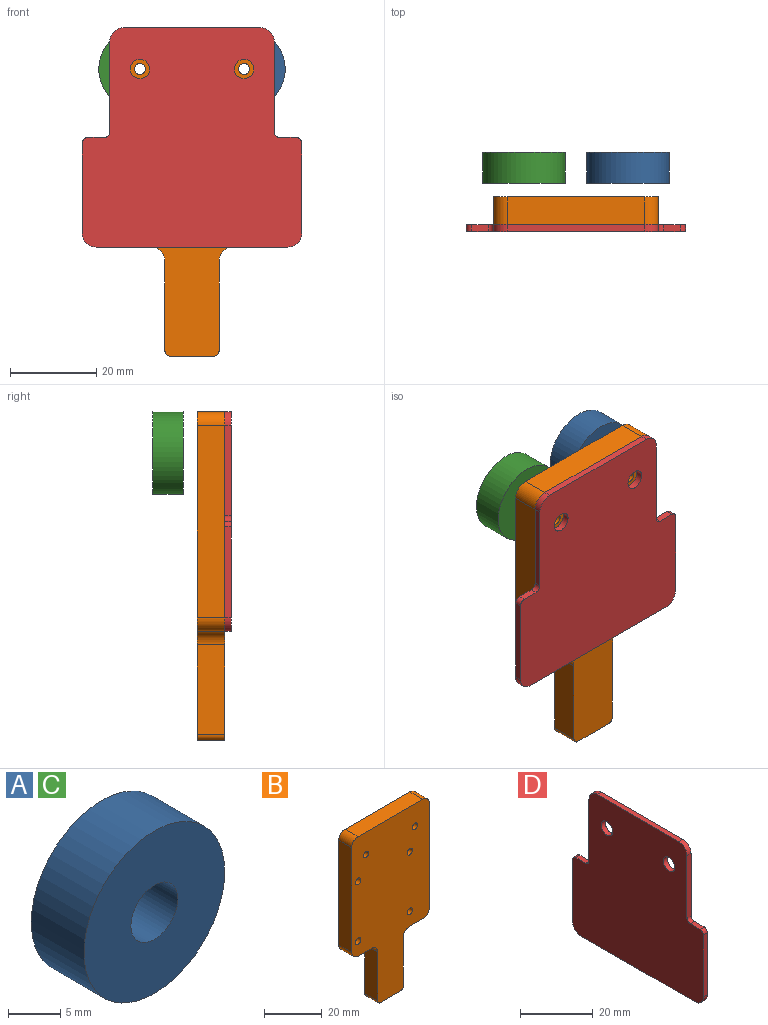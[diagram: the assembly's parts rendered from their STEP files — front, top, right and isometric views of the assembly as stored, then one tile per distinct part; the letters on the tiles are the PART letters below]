
ASSEMBLY  parts=4 mates=3
PART A: 4 faces, bbox 19.1x7.1x19.1 mm
  f0: cylinder r=3.17mm len=7.14mm, axis (0,1,0), area 142.4mm2, adj f2,f3
  f1: cylinder r=9.53mm len=19.05mm, axis (0,1,0), area 427.2mm2, adj f2,f3
  f2: plane 19.05x19.05mm, normal (0,-1,0), area 253.4mm2, adj f0,f1
  f3: plane 19.05x19.05mm, normal (0,1,0), area 253.4mm2, adj f0,f1
PART B: 24 faces, bbox 38.1x6.4x76.1 mm
  f0: cylinder r=3.17mm len=6.35mm, axis (0,1,0), area 31.7mm2, adj f1,f15,f16,f17
  f1: plane 6.41x6.35mm, normal (0,0,-1), area 40.7mm2, adj f0,f2,f16,f17
  f2: cylinder r=3.17mm len=6.35mm, axis (0,1,0), area 31.7mm2, adj f1,f3,f16,f17
  f3: plane 44.45x6.35mm, normal (1,0,0), area 282.3mm2, adj f2,f4,f16,f17
  f4: cylinder r=3.17mm len=6.35mm, axis (0,1,0), area 31.7mm2, adj f3,f5,f16,f17
  f5: plane 31.75x6.35mm, normal (0,0,1), area 201.6mm2, adj f4,f6,f16,f17
  f6: cylinder r=3.17mm len=6.35mm, axis (0,1,0), area 31.7mm2, adj f5,f7,f16,f17
  f7: plane 44.45x6.35mm, normal (-1,0,0), area 282.3mm2, adj f6,f8,f16,f17
  f8: cylinder r=3.17mm len=6.35mm, axis (0,1,0), area 31.7mm2, adj f7,f9,f16,f17
  f9: plane 6.41x6.35mm, normal (0,0,-1), area 40.7mm2, adj f8,f10,f16,f17
  f10: cylinder r=3.17mm len=6.35mm, axis (0,1,0), area 31.7mm2, adj f9,f11,f16,f17
  f11: plane 20.83x6.35mm, normal (-1,0,0), area 132.3mm2, adj f10,f12,f16,f17
  f12: cylinder r=1.27mm len=6.35mm, axis (0,1,0), area 12.7mm2, adj f11,f13,f16,f17
  f13: plane 10.03x6.35mm, normal (0,0,-1), area 63.7mm2, adj f12,f14,f16,f17
  f14: cylinder r=1.27mm len=6.35mm, axis (0,1,0), area 12.7mm2, adj f13,f15,f16,f17
  f15: plane 20.83x6.35mm, normal (1,0,0), area 132.3mm2, adj f0,f14,f16,f17
  f16: plane 76.07x38.1mm, normal (0,-1,0), area 2215.1mm2, adj f0,f1,f2,f3,f4,f5,f6,f7
  f17: plane 76.07x38.1mm, normal (0,1,0), area 2215.1mm2, adj f0,f1,f2,f3,f4,f5,f6,f7
  f18: cylinder r=1.27mm len=6.35mm, axis (0,1,0), area 50.7mm2, adj f16,f17
  f19: cylinder r=1.27mm len=6.35mm, axis (0,1,0), area 50.7mm2, adj f16,f17
  f20: cylinder r=1.35mm len=6.35mm, axis (0,-1,0), area 54mm2, adj f16,f17
  f21: cylinder r=1.35mm len=6.35mm, axis (0,-1,0), area 54mm2, adj f16,f17
  f22: cylinder r=1.35mm len=6.35mm, axis (0,-1,0), area 54mm2, adj f16,f17
  f23: cylinder r=1.35mm len=6.35mm, axis (0,-1,0), area 54mm2, adj f16,f17
PART C: same geometry as A
PART D: 20 faces, bbox 1.6x50.8x50.8 mm
  f0: plane 20.96x1.59mm, normal (0,1,0), area 33.3mm2, adj f1,f15,f16,f17
  f1: cylinder r=3.17mm len=3.18mm, axis (-1,0,0), area 7.9mm2, adj f0,f2,f16,f17
  f2: plane 31.75x1.59mm, normal (0,0,1), area 50.4mm2, adj f1,f3,f16,f17
  f3: cylinder r=3.17mm len=3.18mm, axis (-1,0,0), area 7.9mm2, adj f2,f4,f16,f17
  f4: plane 20.96x1.59mm, normal (0,-1,0), area 33.3mm2, adj f3,f5,f16,f17
  f5: cylinder r=1.27mm len=1.59mm, axis (-1,0,0), area 3.2mm2, adj f4,f6,f16,f17
  f6: plane 3.81x1.59mm, normal (0,0,1), area 6mm2, adj f5,f7,f16,f17
  f7: cylinder r=1.27mm len=1.59mm, axis (-1,0,0), area 3.2mm2, adj f6,f8,f16,f17
  f8: plane 20.96x1.59mm, normal (0,-1,0), area 33.3mm2, adj f7,f9,f16,f17
  f9: cylinder r=3.17mm len=3.18mm, axis (-1,0,0), area 7.9mm2, adj f8,f10,f16,f17
  f10: plane 44.45x1.59mm, normal (0,0,-1), area 70.6mm2, adj f9,f11,f16,f17
  f11: cylinder r=3.17mm len=3.18mm, axis (-1,0,0), area 7.9mm2, adj f10,f12,f16,f17
  f12: plane 20.96x1.59mm, normal (0,1,0), area 33.3mm2, adj f11,f13,f16,f17
  f13: cylinder r=1.27mm len=1.59mm, axis (-1,0,0), area 3.2mm2, adj f12,f14,f16,f17
  f14: plane 3.81x1.59mm, normal (0,0,1), area 6mm2, adj f13,f15,f16,f17
  f15: cylinder r=1.27mm len=1.59mm, axis (-1,0,0), area 3.2mm2, adj f0,f14,f16,f17
  f16: plane 50.8x50.8mm, normal (1,0,0), area 2217.7mm2, adj f0,f1,f2,f3,f4,f5,f6,f7
  f17: plane 50.8x50.8mm, normal (-1,0,0), area 2217.7mm2, adj f0,f1,f2,f3,f4,f5,f6,f7
  f18: cylinder r=2.25mm len=4.5mm, axis (1,0,0), area 22.4mm2, adj f16,f17
  f19: cylinder r=2.25mm len=4.5mm, axis (1,0,0), area 22.4mm2, adj f16,f17
PLACE A t=(12.06,13.49,66.55)mm
PLACE B t=(0,3.18,50.67)mm
PLACE C t=(-12.06,13.49,66.55)mm
PLACE D rot(axis=(0,0,-1),90deg) t=(0,-3.17,50.67)mm
MATE fastened C.f0 <-> B.f19  axis (0,-1,0) through (-12.06,6.35,66.55)mm
MATE fastened B.f19 <-> D.f19  axis (0,-1,0) through (-12.06,-3.17,66.55)mm
MATE fastened B.f18 <-> A.f0  axis (0,1,0) through (12.06,3.18,66.55)mm
